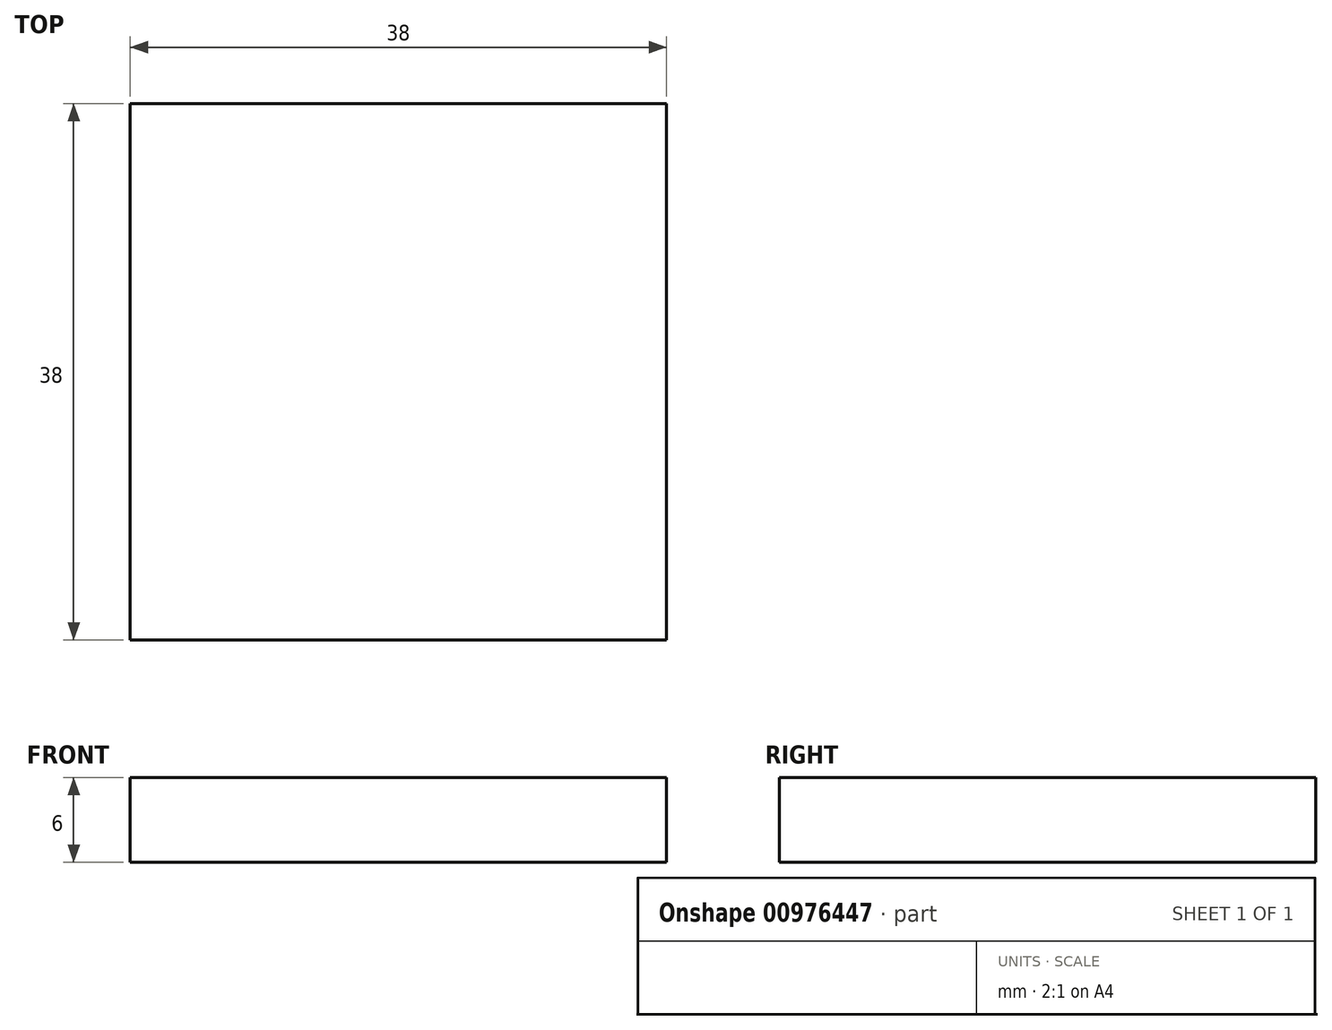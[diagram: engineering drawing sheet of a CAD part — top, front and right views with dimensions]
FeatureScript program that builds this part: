
annotation { "Feature Type Name" : "Feature", "Feature Type Description" : "" }
export const myFeature = defineFeature(function(context is Context, id is Id, definition is map)
    precondition{}
    {
        {
            var Q0;
            Q0=qCreatedBy(makeId("Top.planeOp"),FACE);
            var sketch = newSketch(context, id + "F0", { "sketchPlane" : qUnion([Q0])});
            skLineSegment(sketch, "E0", {"start": v(0, 0) * mm, "end": v(-38, 0) * mm});
            skLineSegment(sketch, "E1", {"start": v(-38, 0) * mm, "end": v(-38, 38) * mm});
            skLineSegment(sketch, "E2", {"start": v(-38, 38) * mm, "end": v(0, 38) * mm});
            skLineSegment(sketch, "E3", {"start": v(0, 38) * mm, "end": v(0, 0) * mm});
            skSolve(sketch);
        }
        {
            var Q0;
            Q0=makeQuery(id+"F0.imprint","IMPRINT",FACE,{"disambiguationData":[TD([[makeQuery(id+"F0.imprint","IMPRINT",EDGE,{"derivedFrom":sQuery(id+"F0.wireOp",EDGE,"E0")}),-1.0]])]});
            extrude(context, id + "F1", {"entities" : qUnion([Q0]), "offsetDistance" : 25 * mm, "depth" : 6 * mm});
        }
    });
